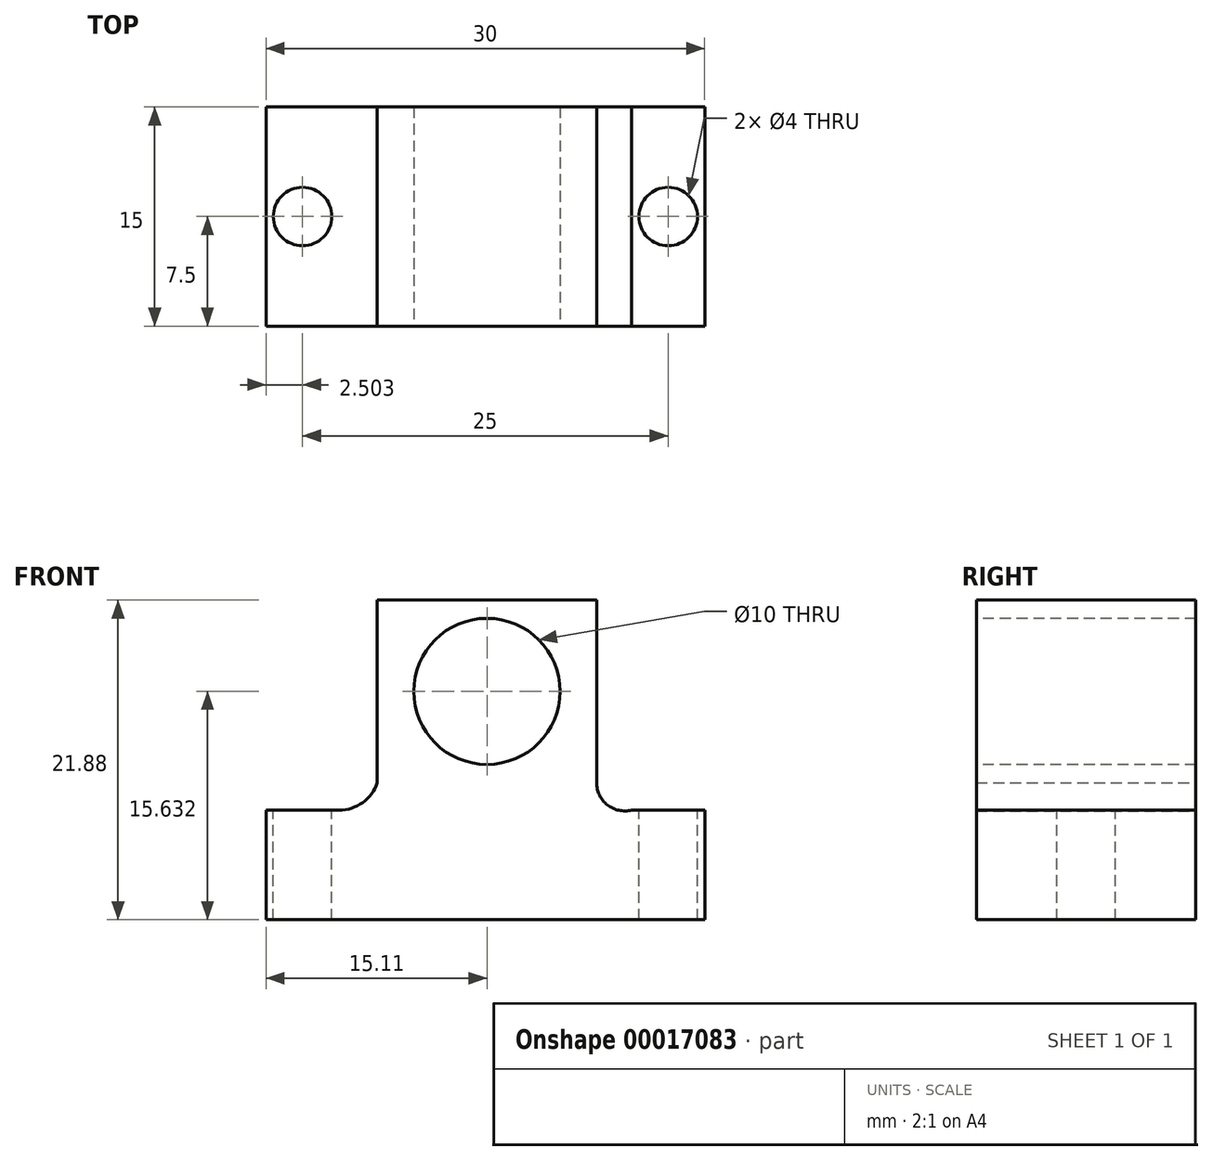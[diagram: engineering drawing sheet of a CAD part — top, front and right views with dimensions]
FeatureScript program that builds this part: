
annotation { "Feature Type Name" : "Feature", "Feature Type Description" : "" }
export const myFeature = defineFeature(function(context is Context, id is Id, definition is map)
    precondition{}
    {
        {
            var Q0;
            Q0=qCreatedBy(makeId("Front.planeOp"),FACE);
            var sketch = newSketch(context, id + "F0", { "sketchPlane" : qUnion([Q0])});
            skLineSegment(sketch, "E0", {"start": v(-19.15, 15.3) * mm, "end": v(-24.15, 15.3) * mm});
            skLineSegment(sketch, "E1", {"start": v(-24.15, 15.3) * mm, "end": v(-24.15, 7.8) * mm});
            skLineSegment(sketch, "E2", {"start": v(-24.15, 7.8) * mm, "end": v(5.85, 7.8) * mm});
            skLineSegment(sketch, "E3", {"start": v(0.85, 15.3) * mm, "end": v(5.85, 15.3) * mm});
            skLineSegment(sketch, "E4", {"start": v(5.85, 15.3) * mm, "end": v(5.85, 7.8) * mm});
            skLineSegment(sketch, "E5", {"start": v(-16.54, 17.17) * mm, "end": v(-16.54, 29.67) * mm});
            skArc(sketch, "E6", {"start": v(-19.15, 15.3) * mm, "mid": v(-17.54, 15.81) * mm, "end": v(-16.54, 17.17) * mm});
            skLineSegment(sketch, "E7", {"start": v(-16.54, 29.67) * mm, "end": v(-1.54, 29.67) * mm});
            skLineSegment(sketch, "E8", {"start": v(-1.54, 17.17) * mm, "end": v(-1.54, 29.67) * mm});
            skArc(sketch, "E9", {"start": v(-1.54, 17.17) * mm, "mid": v(-0.8, 15.65) * mm, "end": v(0.85, 15.3) * mm});
            skSolve(sketch);
        }
        {
            var Q0;
            Q0 = qSketchRegion(id + "F0", true);
            extrude(context, id + "F1", {"entities" : qUnion([Q0]), "depth" : 15 * mm});
        }
        {
            var Q0;
            Q0=makeQuery(id+"F1.opExtrude","SWEPT_FACE",FACE,{"disambiguationData":[OSD([sQuery(id+"F0.wireOp",EDGE,"E3")])]});
            var sketch = newSketch(context, id + "F2", { "sketchPlane" : qUnion([Q0])});
            skCircle(sketch, "E10", {"center": v(3.35, -7.5) * mm, "radius": 2 * mm});
            skCircle(sketch, "E11", {"center": v(-21.59, -7.32) * mm, "radius": 2 * mm});
            skSolve(sketch);
        }
        {
            var Q0;
            Q0=makeQuery(id+"F2.imprint","IMPRINT",FACE,{"disambiguationData":[TD([[makeQuery(id+"F2.imprint","IMPRINT",EDGE,{"derivedFrom":sQuery(id+"F2.wireOp",EDGE,"E10")}),1.0]])]});
            extrude(context, id + "F3", {"entities" : qUnion([Q0]), "operationType" : NewBodyOperationType.REMOVE, "endBound" : BoundingType.THROUGH_ALL, "oppositeDirection" : true, "depth" : 25 * mm});
        }
        {
            var Q0;
            Q0=makeQuery(id+"F1.opExtrude","SWEPT_FACE",FACE,{"disambiguationData":[OSD([sQuery(id+"F0.wireOp",EDGE,"E0")])]});
            var sketch = newSketch(context, id + "F4", { "sketchPlane" : qUnion([Q0])});
            skCircle(sketch, "E12", {"center": v(-21.65, -7.5) * mm, "radius": 2 * mm});
            skSolve(sketch);
        }
        {
            var Q0;
            Q0 = qSketchRegion(id + "F4", true);
            extrude(context, id + "F5", {"entities" : qUnion([Q0]), "operationType" : NewBodyOperationType.REMOVE, "endBound" : BoundingType.THROUGH_ALL, "oppositeDirection" : true, "depth" : 25 * mm});
        }
        {
            var Q0;
            Q0=makeQuery(id+"F1.opExtrude","CAP_FACE",FACE,{"disambiguationData":[OSD([sQuery(id+"F0.wireOp",EDGE,"E0"),sQuery(id+"F0.wireOp",EDGE,"E1"),sQuery(id+"F0.wireOp",EDGE,"E2"),sQuery(id+"F0.wireOp",EDGE,"E3"),sQuery(id+"F0.wireOp",EDGE,"E4"),sQuery(id+"F0.wireOp",EDGE,"E5"),sQuery(id+"F0.wireOp",EDGE,"E6"),sQuery(id+"F0.wireOp",EDGE,"E7"),sQuery(id+"F0.wireOp",EDGE,"E8"),sQuery(id+"F0.wireOp",EDGE,"E9")])],"isStart":false});
            var sketch = newSketch(context, id + "F6", { "sketchPlane" : qUnion([Q0])});
            skCircle(sketch, "E13", {"center": v(-9.04, 23.42) * mm, "radius": 5 * mm});
            skSolve(sketch);
        }
        {
            var Q0;
            Q0 = qSketchRegion(id + "F6", true);
            extrude(context, id + "F7", {"entities" : qUnion([Q0]), "operationType" : NewBodyOperationType.REMOVE, "endBound" : BoundingType.THROUGH_ALL, "oppositeDirection" : true, "depth" : 25 * mm});
        }
    });
